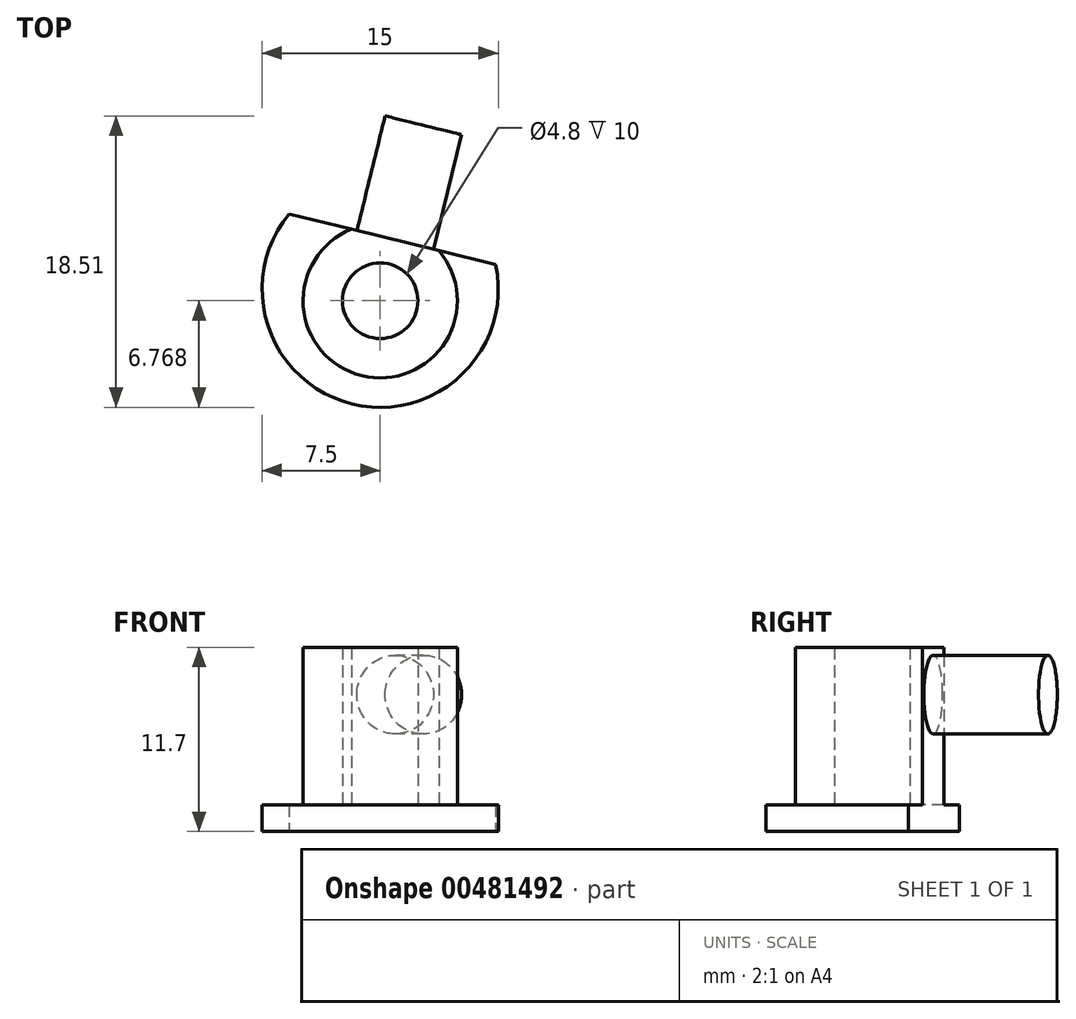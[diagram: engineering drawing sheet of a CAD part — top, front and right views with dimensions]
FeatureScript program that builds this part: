
annotation { "Feature Type Name" : "Feature", "Feature Type Description" : "" }
export const myFeature = defineFeature(function(context is Context, id is Id, definition is map)
    precondition{}
    {
        {
            var Q0;
            Q0=qCreatedBy(makeId("Top.planeOp"),FACE);
            var sketch = newSketch(context, id + "F0", { "sketchPlane" : qUnion([Q0])});
            skArc(sketch, "E0", {"start": v(-5.77, 4.79) * mm, "mid": v(-1.8, -7.28) * mm, "end": v(7.34, 1.56) * mm});
            skLineSegment(sketch, "E1", {"start": v(-5.77, 4.79) * mm, "end": v(7.34, 1.56) * mm});
            skSolve(sketch);
        }
        {
            var Q0;
            Q0=makeQuery(id+"F0.imprint","IMPRINT",FACE,{"disambiguationData":[TD([[makeQuery(id+"F0.imprint","IMPRINT",EDGE,{"derivedFrom":sQuery(id+"F0.wireOp",EDGE,"E0")}),1.0]])]});
            extrude(context, id + "F1", {"entities" : qUnion([Q0]), "depth" : 1.7 * mm});
        }
        {
            var Q0;
            Q0=makeQuery(id+"F1.opExtrude","CAP_FACE",FACE,{"disambiguationData":[OSD([sQuery(id+"F0.wireOp",EDGE,"E0"),sQuery(id+"F0.wireOp",EDGE,"E1")])],"isStart":false});
            var sketch = newSketch(context, id + "F2", { "sketchPlane" : qUnion([Q0])});
            skCircle(sketch, "E2", {"center": v(0, -0.73) * mm, "radius": 4.9 * mm});
            skCircle(sketch, "E3", {"center": v(0, -0.73) * mm, "radius": 2.4 * mm});
            skSolve(sketch);
        }
        {
            var Q0;
            Q0=makeQuery(id+"F2.imprint","IMPRINT",FACE,{"disambiguationData":[TD([[makeQuery(id+"F2.imprint","IMPRINT",EDGE,{"derivedFrom":sQuery(id+"F2.wireOp",EDGE,"E3")}),-1.0]])]});
            extrude(context, id + "F3", {"entities" : qUnion([Q0]), "operationType" : NewBodyOperationType.ADD, "depth" : 10 * mm});
        }
        {
            var Q0;
            {var subQ0=sQuery(id+"F0.wireOp",EDGE,"E1");Q0=makeQuery(id+"F3.boolean.opBoolean","MERGE",FACE,{"derivedFrom":[makeQuery(id+"F1.opExtrude","SWEPT_FACE",FACE,{"disambiguationData":[OSD([subQ0])]}),makeQuery(id+"F3.opExtrude","SWEPT_FACE",FACE,{"disambiguationData":[OSD([subQ0])]})]});}
            var sketch = newSketch(context, id + "F4", { "sketchPlane" : qUnion([Q0])});
            skLineSegment(sketch, "E4", {"start": v(-3.03, 11.7) * mm, "end": v(2.68, 11.7) * mm});
            skPoint(sketch, "E5.endSnap0", {"position": v(-0.17, 11.7) * mm});
            skLineSegment(sketch, "E6", {"start": v(-0.17, 11.7) * mm, "end": v(-0.17, 8.7) * mm});
            skLineSegment(sketch, "E7", {"start": v(-0.17, 11.7) * mm, "end": v(-0.17, 8.7) * mm, "construction": true});
            skCircle(sketch, "E8", {"center": v(-0.17, 8.7) * mm, "radius": 2.5 * mm});
            skSolve(sketch);
        }
        {
            var Q0;
            Q0=makeQuery(id+"F4.imprint","IMPRINT",FACE,{"disambiguationData":[TD([[makeQuery(id+"F4.imprint","IMPRINT",EDGE,{"derivedFrom":sQuery(id+"F4.wireOp",EDGE,"E8")}),1.0]])]});
            extrude(context, id + "F5", {"entities" : qUnion([Q0]), "operationType" : NewBodyOperationType.ADD, "depth" : 7.5 * mm});
        }
    });
